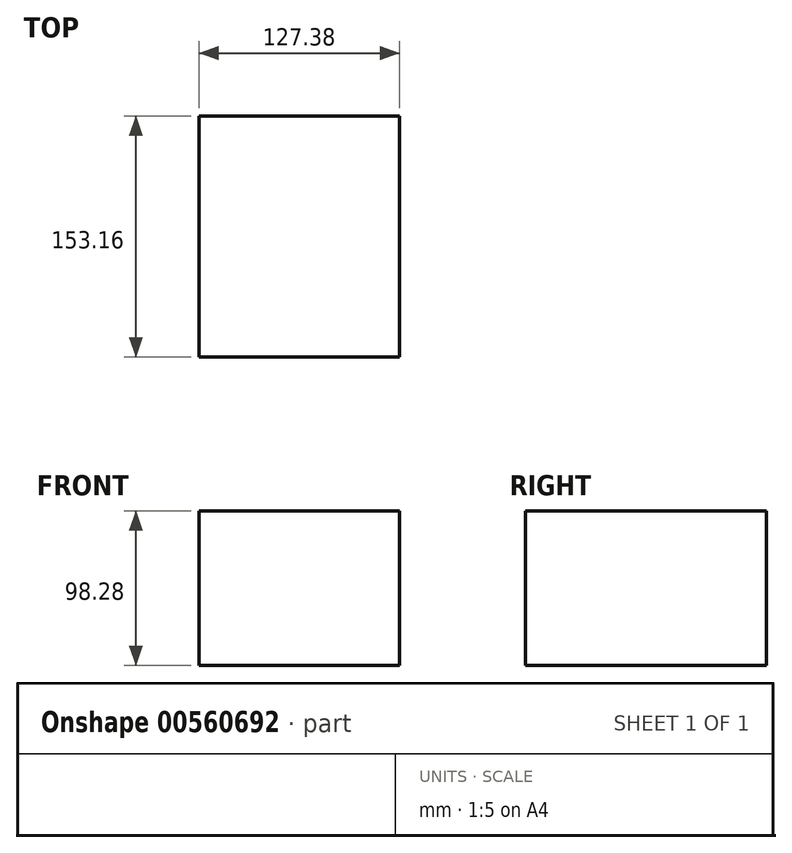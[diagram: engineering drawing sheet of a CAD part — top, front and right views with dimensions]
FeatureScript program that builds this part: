
annotation { "Feature Type Name" : "Feature", "Feature Type Description" : "" }
export const myFeature = defineFeature(function(context is Context, id is Id, definition is map)
    precondition{}
    {
        {
            var Q0;
            Q0=qCreatedBy(makeId("Front.planeOp"),FACE);
            var sketch = newSketch(context, id + "F0", { "sketchPlane" : qUnion([Q0])});
            skLineSegment(sketch, "E0.bottom", {"start": v(63.7, 49.14) * mm, "end": v(-63.7, 49.14) * mm});
            skLineSegment(sketch, "E0.top", {"start": v(63.7, -49.14) * mm, "end": v(-63.7, -49.14) * mm});
            skLineSegment(sketch, "E0.left", {"start": v(63.7, 49.14) * mm, "end": v(63.7, -49.14) * mm});
            skLineSegment(sketch, "E0.right", {"start": v(-63.7, 49.14) * mm, "end": v(-63.7, -49.14) * mm});
            skPoint(sketch, "E0.middle", {"position": v(0, 0) * mm});
            skCircle(sketch, "E1", {"center": v(0, 0) * mm, "radius": 25.08 * mm});
            skSolve(sketch);
        }
        {
            var Q0;
            Q0=makeQuery(id+"F0.imprint","IMPRINT",FACE,{"disambiguationData":[TD([[makeQuery(id+"F0.imprint","IMPRINT",EDGE,{"derivedFrom":sQuery(id+"F0.wireOp",EDGE,"E1")}),1.0]])]});
            extrude(context, id + "F1", {"entities" : qUnion([Q0]), "depth" : 127 * mm, "offsetDistance" : 25.4 * mm});
        }
        {
            var Q0;
            Q0 = qSketchRegion(id + "F0", true);
            extrude(context, id + "F2", {"entities" : qUnion([Q0]), "operationType" : NewBodyOperationType.ADD, "depth" : 25.4 * mm, "offsetDistance" : 25.4 * mm});
        }
        {
            var Q0;
            Q0=makeQuery(id+"F2.opExtrude","CAP_EDGE",EDGE,{"disambiguationData":[OSD([sQuery(id+"F0.wireOp",EDGE,"E1")])],"isStart":false});
            var Q1;
            Q1=makeQuery(id+"F1.opExtrude","CAP_EDGE",EDGE,{"disambiguationData":[OSD([sQuery(id+"F0.wireOp",EDGE,"E1")])],"isStart":false});
            fillet(context, id + "F3", {"entities" : qUnion([Q0, Q1]), "radius" : 5.08 * mm, "tangentPropagation" : true, "allowEdgeOverflow" : false});
        }
        {
            var Q0;
            {var subQ0=sQuery(id+"F0.wireOp",EDGE,"E1");Q0=makeQuery(id+"F2.boolean.opBoolean","MERGE",FACE,{"derivedFrom":[makeQuery(id+"F1.opExtrude","CAP_FACE",FACE,{"disambiguationData":[OSD([subQ0])],"isStart":true}),makeQuery(id+"F2.opExtrude","CAP_FACE",FACE,{"disambiguationData":[OSD([sQuery(id+"F0.wireOp",EDGE,"E0.bottom"),sQuery(id+"F0.wireOp",EDGE,"E0.top"),sQuery(id+"F0.wireOp",EDGE,"E0.left"),sQuery(id+"F0.wireOp",EDGE,"E0.right"),subQ0])],"isStart":true})]});}
            extrude(context, id + "F4", {"entities" : qUnion([Q0]), "operationType" : NewBodyOperationType.ADD, "oppositeDirection" : true, "depth" : 153.16 * mm, "offsetDistance" : 25.4 * mm});
        }
    });
